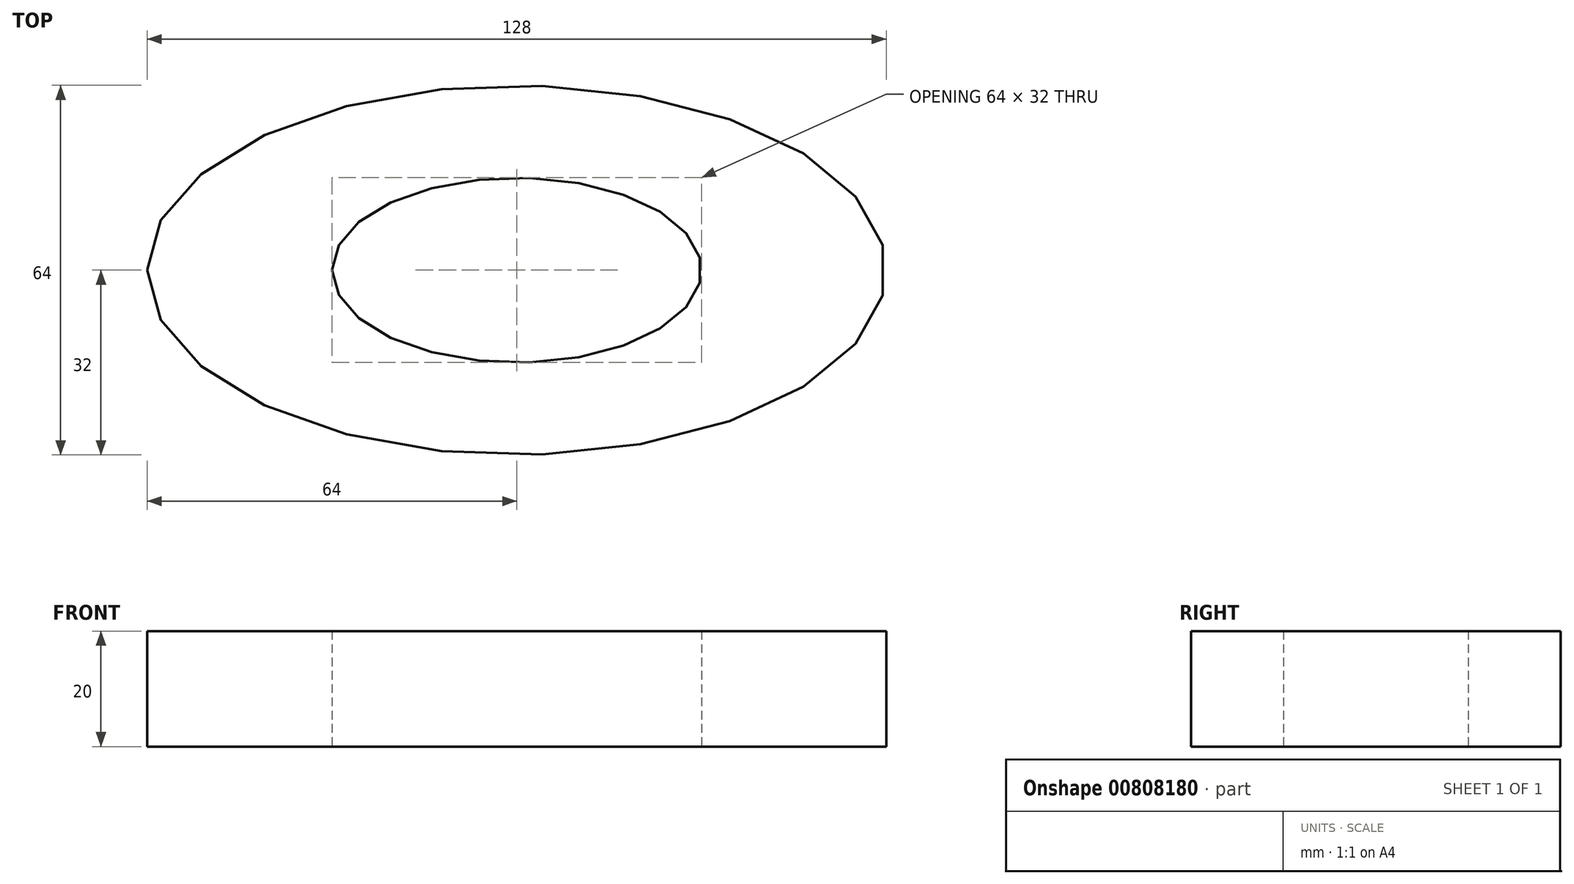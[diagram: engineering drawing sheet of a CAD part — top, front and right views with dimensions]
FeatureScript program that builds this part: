
annotation { "Feature Type Name" : "Feature", "Feature Type Description" : "" }
export const myFeature = defineFeature(function(context is Context, id is Id, definition is map)
    precondition{}
    {
        {
            var Q0;
            Q0=qCreatedBy(makeId("Top.planeOp"),FACE);
            var sketch = newSketch(context, id + "F0", { "sketchPlane" : qUnion([Q0])});
            skEllipse(sketch, "E0", {"center": v(0, 0) * mm, "majorRadius": 64 * mm, "minorRadius": 32 * mm, "majorAxis": v(-1, 0)});
            skEllipse(sketch, "E1", {"center": v(0, 0) * mm, "majorRadius": 32 * mm, "minorRadius": 16 * mm, "majorAxis": v(-1, 0)});
            skSolve(sketch);
        }
        {
            var Q0;
            Q0=makeQuery(id+"F0.imprint","IMPRINT",FACE,{"disambiguationData":[TD([[makeQuery(id+"F0.imprint","IMPRINT",EDGE,{"derivedFrom":sQuery(id+"F0.wireOp",EDGE,"E0")}),1.0]])]});
            extrude(context, id + "F1", {"entities" : qUnion([Q0]), "depth" : 20 * mm, "offsetDistance" : 25 * mm});
        }
    });
